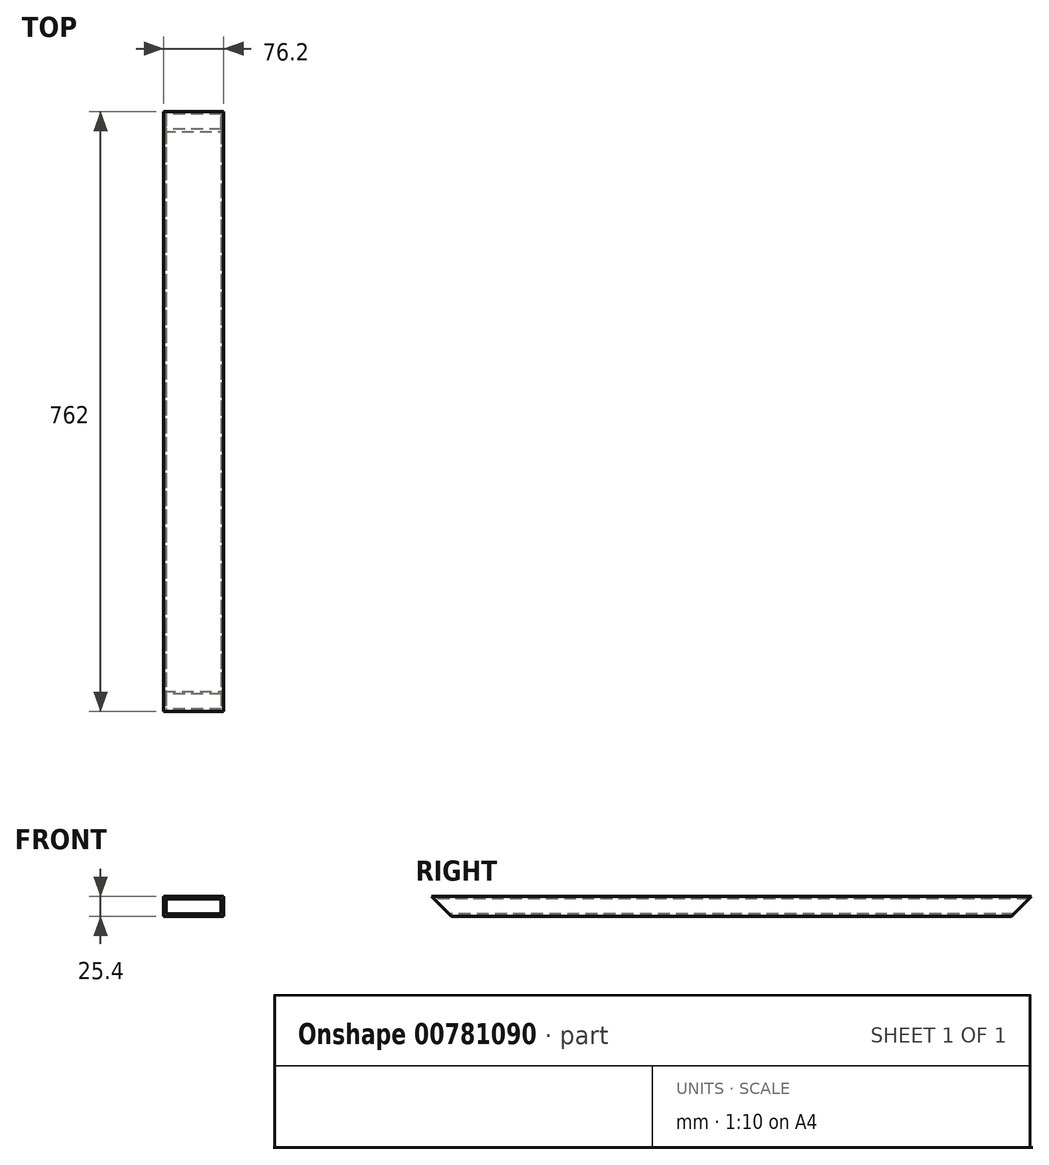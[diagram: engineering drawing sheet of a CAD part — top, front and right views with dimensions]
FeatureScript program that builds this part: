
annotation { "Feature Type Name" : "Feature", "Feature Type Description" : "" }
export const myFeature = defineFeature(function(context is Context, id is Id, definition is map)
    precondition{}
    {
        {
            var Q0;
            Q0=qCreatedBy(makeId("Front.planeOp"),FACE);
            var sketch = newSketch(context, id + "F0", { "sketchPlane" : qUnion([Q0])});
            skLineSegment(sketch, "E0.bottom", {"start": v(0, 0) * mm, "end": v(76.2, 0) * mm});
            skLineSegment(sketch, "E0.top", {"start": v(0, -25.4) * mm, "end": v(76.2, -25.4) * mm});
            skLineSegment(sketch, "E0.left", {"start": v(0, 0) * mm, "end": v(0, -25.4) * mm});
            skLineSegment(sketch, "E0.right", {"start": v(76.2, 0) * mm, "end": v(76.2, -25.4) * mm});
            skLineSegment(sketch, "E1.bottom", {"start": v(3.17, -3.18) * mm, "end": v(73.03, -3.18) * mm});
            skLineSegment(sketch, "E1.top", {"start": v(3.17, -22.23) * mm, "end": v(73.03, -22.23) * mm});
            skLineSegment(sketch, "E1.left", {"start": v(3.17, -3.18) * mm, "end": v(3.17, -22.23) * mm});
            skLineSegment(sketch, "E1.right", {"start": v(73.03, -3.18) * mm, "end": v(73.03, -22.23) * mm});
            skSolve(sketch);
        }
        {
            var Q0;
            Q0=makeQuery(id+"F0.imprint","IMPRINT",FACE,{"disambiguationData":[TD([[makeQuery(id+"F0.imprint","IMPRINT",EDGE,{"derivedFrom":sQuery(id+"F0.wireOp",EDGE,"E0.bottom")}),-1.0]])]});
            extrude(context, id + "F1", {"entities" : qUnion([Q0]), "oppositeDirection" : true, "depth" : 381 * mm, "offsetDistance" : 25.4 * mm, "hasSecondDirection" : true, "secondDirectionOppositeDirection" : false, "secondDirectionDepth" : 381 * mm});
        }
        {
            var Q0;
            Q0=makeQuery(id+"F1.opExtrude","SWEPT_FACE",FACE,{"disambiguationData":[OSD([sQuery(id+"F0.wireOp",EDGE,"E0.right")])]});
            var sketch = newSketch(context, id + "F2", { "sketchPlane" : qUnion([Q0])});
            skLineSegment(sketch, "E2", {"start": v(-381, 0) * mm, "end": v(-355.6, -25.4) * mm});
            skLineSegment(sketch, "E3", {"start": v(-355.6, -25.4) * mm, "end": v(-381, -25.4) * mm});
            skLineSegment(sketch, "E4", {"start": v(-381, -25.4) * mm, "end": v(-381, 0) * mm});
            skLineSegment(sketch, "E5.MirrorCS", {"start": v(381, 0) * mm, "end": v(355.6, -25.4) * mm});
            skLineSegment(sketch, "E6.MirrorCS", {"start": v(381, -25.4) * mm, "end": v(381, 0) * mm});
            skLineSegment(sketch, "E7.MirrorCS", {"start": v(355.6, -25.4) * mm, "end": v(381, -25.4) * mm});
            skSolve(sketch);
        }
        {
            var Q0;
            Q0=makeQuery(id+"F2.imprint","IMPRINT",FACE,{"disambiguationData":[TD([[makeQuery(id+"F2.imprint","IMPRINT",EDGE,{"derivedFrom":sQuery(id+"F2.wireOp",EDGE,"E2")}),-1.0]])]});
            var Q1;
            Q1=makeQuery(id+"F2.imprint","IMPRINT",FACE,{"disambiguationData":[TD([[makeQuery(id+"F2.imprint","IMPRINT",EDGE,{"derivedFrom":sQuery(id+"F2.wireOp",EDGE,"E5.MirrorCS")}),1.0]])]});
            extrude(context, id + "F3", {"entities" : qUnion([Q0, Q1]), "operationType" : NewBodyOperationType.REMOVE, "endBound" : BoundingType.THROUGH_ALL, "oppositeDirection" : true, "depth" : 25.4 * mm, "offsetDistance" : 25.4 * mm});
        }
    });
